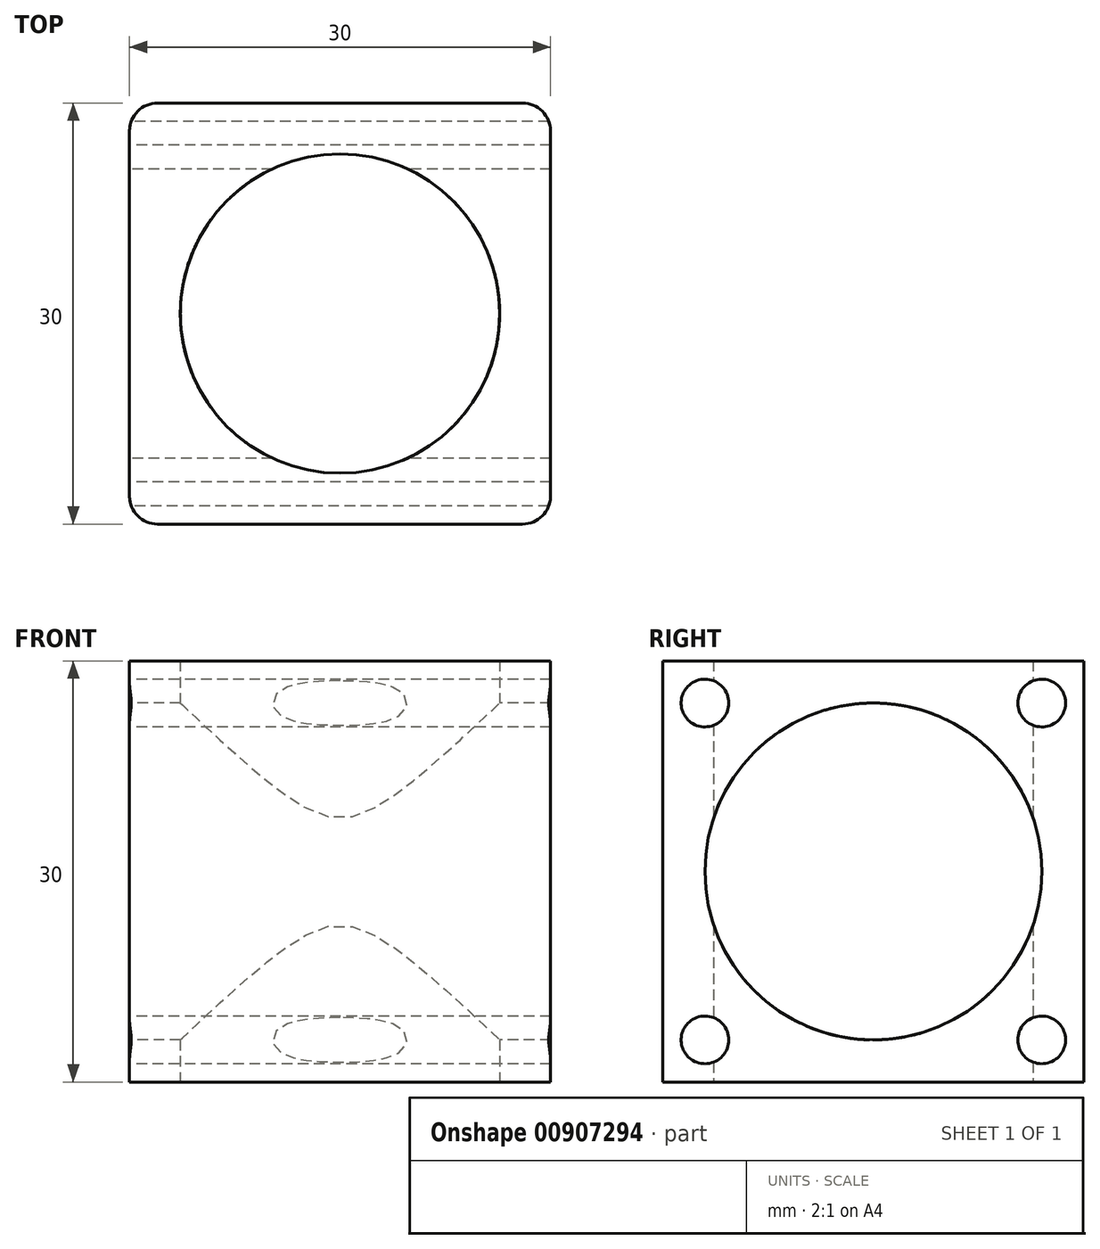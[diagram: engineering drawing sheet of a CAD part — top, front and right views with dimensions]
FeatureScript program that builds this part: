
annotation { "Feature Type Name" : "Feature", "Feature Type Description" : "" }
export const myFeature = defineFeature(function(context is Context, id is Id, definition is map)
    precondition{}
    {
        {
            var Q0;
            Q0=qCreatedBy(makeId("Top.planeOp"),FACE);
            var sketch = newSketch(context, id + "F0", { "sketchPlane" : qUnion([Q0])});
            skLineSegment(sketch, "E0.bottom", {"start": v(15, -15) * mm, "end": v(-15, -15) * mm});
            skLineSegment(sketch, "E0.top", {"start": v(15, 15) * mm, "end": v(-15, 15) * mm});
            skLineSegment(sketch, "E0.left", {"start": v(15, -15) * mm, "end": v(15, 15) * mm});
            skLineSegment(sketch, "E0.right", {"start": v(-15, -15) * mm, "end": v(-15, 15) * mm});
            skPoint(sketch, "E0.middle", {"position": v(0, 0) * mm});
            skCircle(sketch, "E1", {"center": v(0, 0) * mm, "radius": 11.38 * mm});
            skSolve(sketch);
        }
        {
            var Q0;
            Q0=qSketchRegion(id+"F0",true);
            extrude(context, id + "F1", {"entities" : qUnion([Q0]), "depth" : 30 * mm, "offsetDistance" : 25 * mm});
        }
        {
            var Q0;
            Q0=makeQuery(id+"F1.opExtrude","SWEPT_FACE",FACE,{"disambiguationData":[OSD([sQuery(id+"F0.wireOp",EDGE,"E0.right")])]});
            var sketch = newSketch(context, id + "F2", { "sketchPlane" : qUnion([Q0])});
            skLineSegment(sketch, "E2", {"start": v(0, 0) * mm, "end": v(0, 30) * mm, "construction": true});
            skLineSegment(sketch, "E3", {"start": v(-15, 15) * mm, "end": v(15, 15) * mm, "construction": true});
            skLineSegment(sketch, "E4.bottom", {"start": v(12, 3) * mm, "end": v(-12, 3) * mm, "construction": true});
            skLineSegment(sketch, "E4.top", {"start": v(12, 27) * mm, "end": v(-12, 27) * mm, "construction": true});
            skLineSegment(sketch, "E4.left", {"start": v(12, 3) * mm, "end": v(12, 27) * mm, "construction": true});
            skLineSegment(sketch, "E4.right", {"start": v(-12, 3) * mm, "end": v(-12, 27) * mm, "construction": true});
            skPoint(sketch, "E4.middle", {"position": v(0, 15) * mm});
            skCircle(sketch, "E5", {"center": v(0, 15) * mm, "radius": 12 * mm});
            skSolve(sketch);
        }
        {
            var Q0;
            Q0=sQuery(id+"F2.wireOp",VERTEX,"E4.top.end");
            var Q1;
            Q1=sQuery(id+"F2.wireOp",VERTEX,"E4.top.start");
            var Q2;
            Q2=sQuery(id+"F2.wireOp",VERTEX,"E4.bottom.start");
            var Q3;
            Q3=sQuery(id+"F2.wireOp",VERTEX,"E4.bottom.end");
            var Q4;
            Q4=makeQuery(id+"F1.opExtrude","SWEPT_BODY",BODY,{"disambiguationData":[OSD([sQuery(id+"F0.wireOp",EDGE,"E0.bottom"),sQuery(id+"F0.wireOp",EDGE,"E0.top"),sQuery(id+"F0.wireOp",EDGE,"E0.left"),sQuery(id+"F0.wireOp",EDGE,"E0.right"),sQuery(id+"F0.wireOp",EDGE,"E1")])]});
            hole(context, id + "F3", {"style" : HoleStyle.SIMPLE, "endStyle" : HoleEndStyle.THROUGH, "holeDiameter" : 3.4 * mm, "majorDiameter" : 5 * mm, "isTappedThrough" : true, "tappedDepth" : 12 * mm, "tapClearance" : 3, "locations" : qUnion([Q0, Q1, Q2, Q3]), "scope" : qUnion([Q4])});
        }
        {
            var Q0;
            Q0=makeQuery(id+"F1.opExtrude","SWEPT_EDGE",EDGE,{"disambiguationData":[OSD([sQuery(id+"F0.wireOp",EDGE,"E0.top"),sQuery(id+"F0.wireOp",EDGE,"E0.left")])]});
            var Q1;
            Q1=makeQuery(id+"F1.opExtrude","SWEPT_EDGE",EDGE,{"disambiguationData":[OSD([sQuery(id+"F0.wireOp",EDGE,"E0.top"),sQuery(id+"F0.wireOp",EDGE,"E0.right")])]});
            var Q2;
            Q2=makeQuery(id+"F1.opExtrude","SWEPT_EDGE",EDGE,{"disambiguationData":[OSD([sQuery(id+"F0.wireOp",EDGE,"E0.bottom"),sQuery(id+"F0.wireOp",EDGE,"E0.right")])]});
            var Q3;
            Q3=makeQuery(id+"F1.opExtrude","SWEPT_EDGE",EDGE,{"disambiguationData":[OSD([sQuery(id+"F0.wireOp",EDGE,"E0.bottom"),sQuery(id+"F0.wireOp",EDGE,"E0.left")])]});
            fillet(context, id + "F4", {"entities" : qUnion([Q0, Q1, Q2, Q3]), "radius" : 2 * mm, "tangentPropagation" : true, "allowEdgeOverflow" : false});
        }
        {
            var Q0;
            Q0=makeQuery(id+"F2.imprint","IMPRINT",FACE,{"disambiguationData":[TD([[makeQuery(id+"F2.imprint","IMPRINT",EDGE,{"derivedFrom":sQuery(id+"F2.wireOp",EDGE,"E5")}),1.0]])]});
            extrude(context, id + "F5", {"entities" : qUnion([Q0]), "operationType" : NewBodyOperationType.REMOVE, "endBound" : BoundingType.THROUGH_ALL, "oppositeDirection" : true, "depth" : 25 * mm, "offsetDistance" : 25 * mm});
        }
    });
